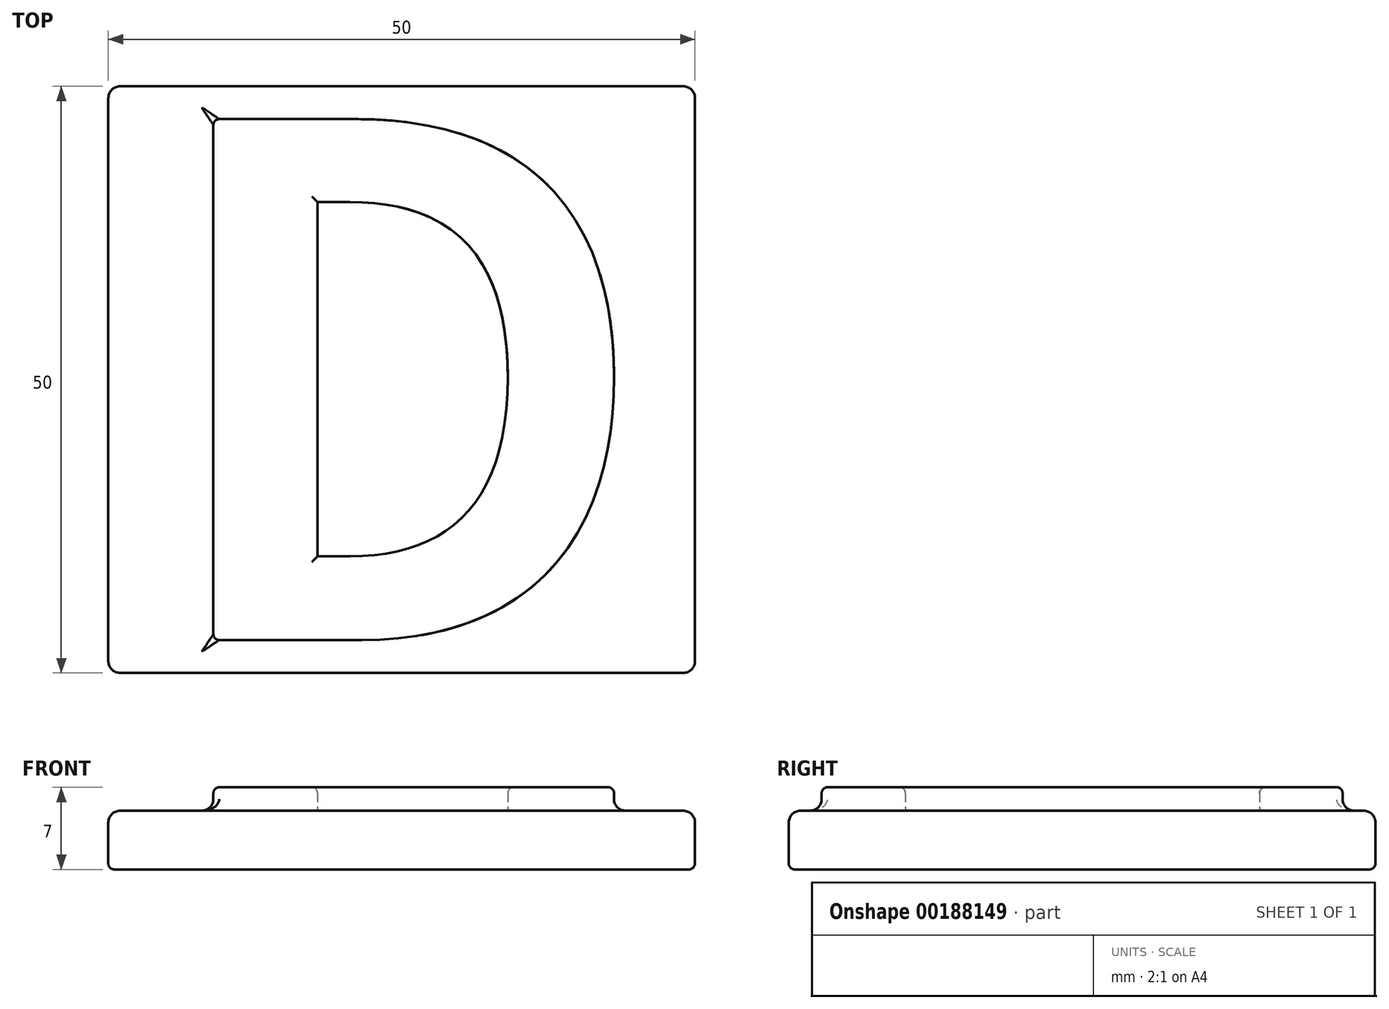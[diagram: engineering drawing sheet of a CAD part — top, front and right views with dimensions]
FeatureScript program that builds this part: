
annotation { "Feature Type Name" : "Feature", "Feature Type Description" : "" }
export const myFeature = defineFeature(function(context is Context, id is Id, definition is map)
    precondition{}
    {
        {
            var Q0;
            Q0=qCreatedBy(makeId("Top.planeOp"),FACE);
            var sketch = newSketch(context, id + "F0", { "sketchPlane" : qUnion([Q0])});
            skLineSegment(sketch, "E0.bottom", {"start": v(25, -25) * mm, "end": v(-25, -25) * mm});
            skLineSegment(sketch, "E0.top", {"start": v(25, 25) * mm, "end": v(-25, 25) * mm});
            skLineSegment(sketch, "E0.left", {"start": v(25, -25) * mm, "end": v(25, 25) * mm});
            skLineSegment(sketch, "E0.right", {"start": v(-25, -25) * mm, "end": v(-25, 25) * mm});
            skPoint(sketch, "E0.middle", {"position": v(0, 0) * mm});
            skSolve(sketch);
        }
        {
            var Q0;
            Q0=makeQuery(id+"F0.imprint","IMPRINT",FACE,{"disambiguationData":[TD([[makeQuery(id+"F0.imprint","IMPRINT",EDGE,{"derivedFrom":sQuery(id+"F0.wireOp",EDGE,"E0.bottom")}),-1.0]])]});
            extrude(context, id + "F1", {"entities" : qUnion([Q0]), "depth" : 5 * mm});
        }
        {
            var Q0;
            Q0=qCreatedBy(makeId("Top.planeOp"),FACE);
            var sketch = newSketch(context, id + "F2", { "sketchPlane" : qUnion([Q0])});
            skText(sketch, "E1", { "text": "D", "fontName": "NotoSansCJKsc-Bold.otf"});
            const initialGuessF2  = {"E1": [-0.0215, -0.0222, 1, 0, 0.0432]};
            skSetInitialGuess(sketch, initialGuessF2);
            skSolve(sketch);
        }
        {
            var Q0;
            Q0 = qSketchRegion(id + "F2", true);
            extrude(context, id + "F3", {"entities" : qUnion([Q0]), "operationType" : NewBodyOperationType.ADD, "depth" : 7 * mm});
        }
        {
            var Q0;
            Q0=makeQuery(id+"F1.opExtrude","CAP_EDGE",EDGE,{"disambiguationData":[OSD([sQuery(id+"F0.wireOp",EDGE,"E0.top")])],"isStart":false});
            var Q1;
            Q1=makeQuery(id+"F1.opExtrude","CAP_EDGE",EDGE,{"disambiguationData":[OSD([sQuery(id+"F0.wireOp",EDGE,"E0.left")])],"isStart":false});
            var Q2;
            Q2=makeQuery(id+"F1.opExtrude","CAP_EDGE",EDGE,{"disambiguationData":[OSD([sQuery(id+"F0.wireOp",EDGE,"E0.bottom")])],"isStart":false});
            var Q3;
            Q3=makeQuery(id+"F1.opExtrude","CAP_EDGE",EDGE,{"disambiguationData":[OSD([sQuery(id+"F0.wireOp",EDGE,"E0.right")])],"isStart":false});
            var Q4;
            Q4=makeQuery(id+"F1.opExtrude","SWEPT_EDGE",EDGE,{"disambiguationData":[OSD([sQuery(id+"F0.wireOp",EDGE,"E0.bottom"),sQuery(id+"F0.wireOp",EDGE,"E0.right")])]});
            var Q5;
            Q5=makeQuery(id+"F1.opExtrude","SWEPT_EDGE",EDGE,{"disambiguationData":[OSD([sQuery(id+"F0.wireOp",EDGE,"E0.bottom"),sQuery(id+"F0.wireOp",EDGE,"E0.left")])]});
            var Q6;
            Q6=makeQuery(id+"F1.opExtrude","SWEPT_EDGE",EDGE,{"disambiguationData":[OSD([sQuery(id+"F0.wireOp",EDGE,"E0.top"),sQuery(id+"F0.wireOp",EDGE,"E0.right")])]});
            var Q7;
            Q7=makeQuery(id+"F1.opExtrude","SWEPT_EDGE",EDGE,{"disambiguationData":[OSD([sQuery(id+"F0.wireOp",EDGE,"E0.top"),sQuery(id+"F0.wireOp",EDGE,"E0.left")])]});
            fillet(context, id + "F4", {"entities" : qUnion([Q0, Q1, Q2, Q3, Q4, Q5, Q6, Q7]), "radius" : 1 * mm, "tangentPropagation" : true, "allowEdgeOverflow" : false});
        }
        {
            var Q0;
            Q0=makeQuery(id+"F3.opExtrude","CAP_EDGE",EDGE,{"disambiguationData":[OSD([sQuery(id+"F2.wireOp",EDGE,"E1.sketch_text.stroke-4")])],"isStart":false});
            var Q1;
            Q1=makeQuery(id+"F3.opExtrude","CAP_EDGE",EDGE,{"disambiguationData":[OSD([sQuery(id+"F2.wireOp",EDGE,"E1.sketch_text.stroke-3")])],"isStart":false});
            var Q2;
            Q2=makeQuery(id+"F3.opExtrude","CAP_EDGE",EDGE,{"disambiguationData":[OSD([sQuery(id+"F2.wireOp",EDGE,"E1.sketch_text.stroke-2")])],"isStart":false});
            var Q3;
            Q3=makeQuery(id+"F3.opExtrude","CAP_EDGE",EDGE,{"disambiguationData":[OSD([sQuery(id+"F2.wireOp",EDGE,"E1.sketch_text.stroke-1")])],"isStart":false});
            var Q4;
            Q4=makeQuery(id+"F3.opExtrude","CAP_EDGE",EDGE,{"disambiguationData":[OSD([sQuery(id+"F2.wireOp",EDGE,"E1.sketch_text.stroke-0")])],"isStart":false});
            var Q5;
            Q5=makeQuery(id+"F3.opExtrude","CAP_EDGE",EDGE,{"disambiguationData":[OSD([sQuery(id+"F2.wireOp",EDGE,"E1.sketch_text.stroke-5")])],"isStart":false});
            var Q6;
            Q6=makeQuery(id+"F3.opExtrude","CAP_EDGE",EDGE,{"disambiguationData":[OSD([sQuery(id+"F2.wireOp",EDGE,"E1.sketch_text.stroke-7")])],"isStart":false});
            var Q7;
            Q7=makeQuery(id+"F3.opExtrude","CAP_EDGE",EDGE,{"disambiguationData":[OSD([sQuery(id+"F2.wireOp",EDGE,"E1.sketch_text.stroke-6")])],"isStart":false});
            var Q8;
            Q8=makeQuery(id+"F3.opExtrude","CAP_EDGE",EDGE,{"disambiguationData":[OSD([sQuery(id+"F2.wireOp",EDGE,"E1.sketch_text.stroke-8")])],"isStart":false});
            var Q9;
            Q9=makeQuery(id+"F3.opExtrude","CAP_EDGE",EDGE,{"disambiguationData":[OSD([sQuery(id+"F2.wireOp",EDGE,"E1.sketch_text.stroke-9")])],"isStart":false});
            fillet(context, id + "F5", {"entities" : qUnion([Q0, Q1, Q2, Q3, Q4, Q5, Q6, Q7, Q8, Q9]), "radius" : 0.5 * mm, "tangentPropagation" : true, "allowEdgeOverflow" : false});
        }
        {
            var Q0;
            Q0=makeQuery(id+"F3.boolean.opBoolean","INTERSECT",EDGE,{"derivedFrom":[makeQuery(id+"F1.opExtrude","CAP_FACE",FACE,{"disambiguationData":[OSD([sQuery(id+"F0.wireOp",EDGE,"E0.bottom"),sQuery(id+"F0.wireOp",EDGE,"E0.top"),sQuery(id+"F0.wireOp",EDGE,"E0.left"),sQuery(id+"F0.wireOp",EDGE,"E0.right")])],"isStart":false}),makeQuery(id+"F3.opExtrude","SWEPT_FACE",FACE,{"disambiguationData":[OSD([sQuery(id+"F2.wireOp",EDGE,"E1.sketch_text.stroke-4")])]})]});
            var Q1;
            Q1=makeQuery(id+"F3.boolean.opBoolean","INTERSECT",EDGE,{"derivedFrom":[makeQuery(id+"F1.opExtrude","CAP_FACE",FACE,{"disambiguationData":[OSD([sQuery(id+"F0.wireOp",EDGE,"E0.bottom"),sQuery(id+"F0.wireOp",EDGE,"E0.top"),sQuery(id+"F0.wireOp",EDGE,"E0.left"),sQuery(id+"F0.wireOp",EDGE,"E0.right")])],"isStart":false}),makeQuery(id+"F3.opExtrude","SWEPT_FACE",FACE,{"disambiguationData":[OSD([sQuery(id+"F2.wireOp",EDGE,"E1.sketch_text.stroke-0")])]})]});
            var Q2;
            Q2=makeQuery(id+"F3.boolean.opBoolean","INTERSECT",EDGE,{"derivedFrom":[makeQuery(id+"F1.opExtrude","CAP_FACE",FACE,{"disambiguationData":[OSD([sQuery(id+"F0.wireOp",EDGE,"E0.bottom"),sQuery(id+"F0.wireOp",EDGE,"E0.top"),sQuery(id+"F0.wireOp",EDGE,"E0.left"),sQuery(id+"F0.wireOp",EDGE,"E0.right")])],"isStart":false}),makeQuery(id+"F3.opExtrude","SWEPT_FACE",FACE,{"disambiguationData":[OSD([sQuery(id+"F2.wireOp",EDGE,"E1.sketch_text.stroke-1")])]})]});
            var Q3;
            Q3=makeQuery(id+"F3.boolean.opBoolean","INTERSECT",EDGE,{"derivedFrom":[makeQuery(id+"F1.opExtrude","CAP_FACE",FACE,{"disambiguationData":[OSD([sQuery(id+"F0.wireOp",EDGE,"E0.bottom"),sQuery(id+"F0.wireOp",EDGE,"E0.top"),sQuery(id+"F0.wireOp",EDGE,"E0.left"),sQuery(id+"F0.wireOp",EDGE,"E0.right")])],"isStart":false}),makeQuery(id+"F3.opExtrude","SWEPT_FACE",FACE,{"disambiguationData":[OSD([sQuery(id+"F2.wireOp",EDGE,"E1.sketch_text.stroke-3")])]})]});
            var Q4;
            Q4=makeQuery(id+"F3.boolean.opBoolean","INTERSECT",EDGE,{"derivedFrom":[makeQuery(id+"F1.opExtrude","CAP_FACE",FACE,{"disambiguationData":[OSD([sQuery(id+"F0.wireOp",EDGE,"E0.bottom"),sQuery(id+"F0.wireOp",EDGE,"E0.top"),sQuery(id+"F0.wireOp",EDGE,"E0.left"),sQuery(id+"F0.wireOp",EDGE,"E0.right")])],"isStart":false}),makeQuery(id+"F3.opExtrude","SWEPT_FACE",FACE,{"disambiguationData":[OSD([sQuery(id+"F2.wireOp",EDGE,"E1.sketch_text.stroke-2")])]})]});
            fillet(context, id + "F6", {"entities" : qUnion([Q0, Q1, Q2, Q3, Q4]), "radius" : 1 * mm, "tangentPropagation" : true, "allowEdgeOverflow" : false});
        }
        {
            var Q0;
            Q0=makeQuery(id+"F3.opExtrude","SWEPT_EDGE",EDGE,{"disambiguationData":[OSD([sQuery(id+"F2.wireOp",EDGE,"E1.sketch_text.stroke-3"),sQuery(id+"F2.wireOp",EDGE,"E1.sketch_text.stroke-4")])]});
            var Q1;
            Q1=makeQuery(id+"F3.opExtrude","SWEPT_EDGE",EDGE,{"disambiguationData":[OSD([sQuery(id+"F2.wireOp",EDGE,"E1.sketch_text.stroke-0"),sQuery(id+"F2.wireOp",EDGE,"E1.sketch_text.stroke-4")])]});
            fillet(context, id + "F7", {"entities" : qUnion([Q0, Q1]), "radius" : 0.5 * mm, "tangentPropagation" : true, "allowEdgeOverflow" : false});
        }
        {
            var Q0;
            Q0=makeQuery(id+"F1.opExtrude","CAP_FACE",FACE,{"disambiguationData":[OSD([sQuery(id+"F0.wireOp",EDGE,"E0.bottom"),sQuery(id+"F0.wireOp",EDGE,"E0.top"),sQuery(id+"F0.wireOp",EDGE,"E0.left"),sQuery(id+"F0.wireOp",EDGE,"E0.right")])],"isStart":true});
            fillet(context, id + "F8", {"entities" : qUnion([Q0]), "radius" : 0.5 * mm, "tangentPropagation" : true, "allowEdgeOverflow" : false});
        }
    });
